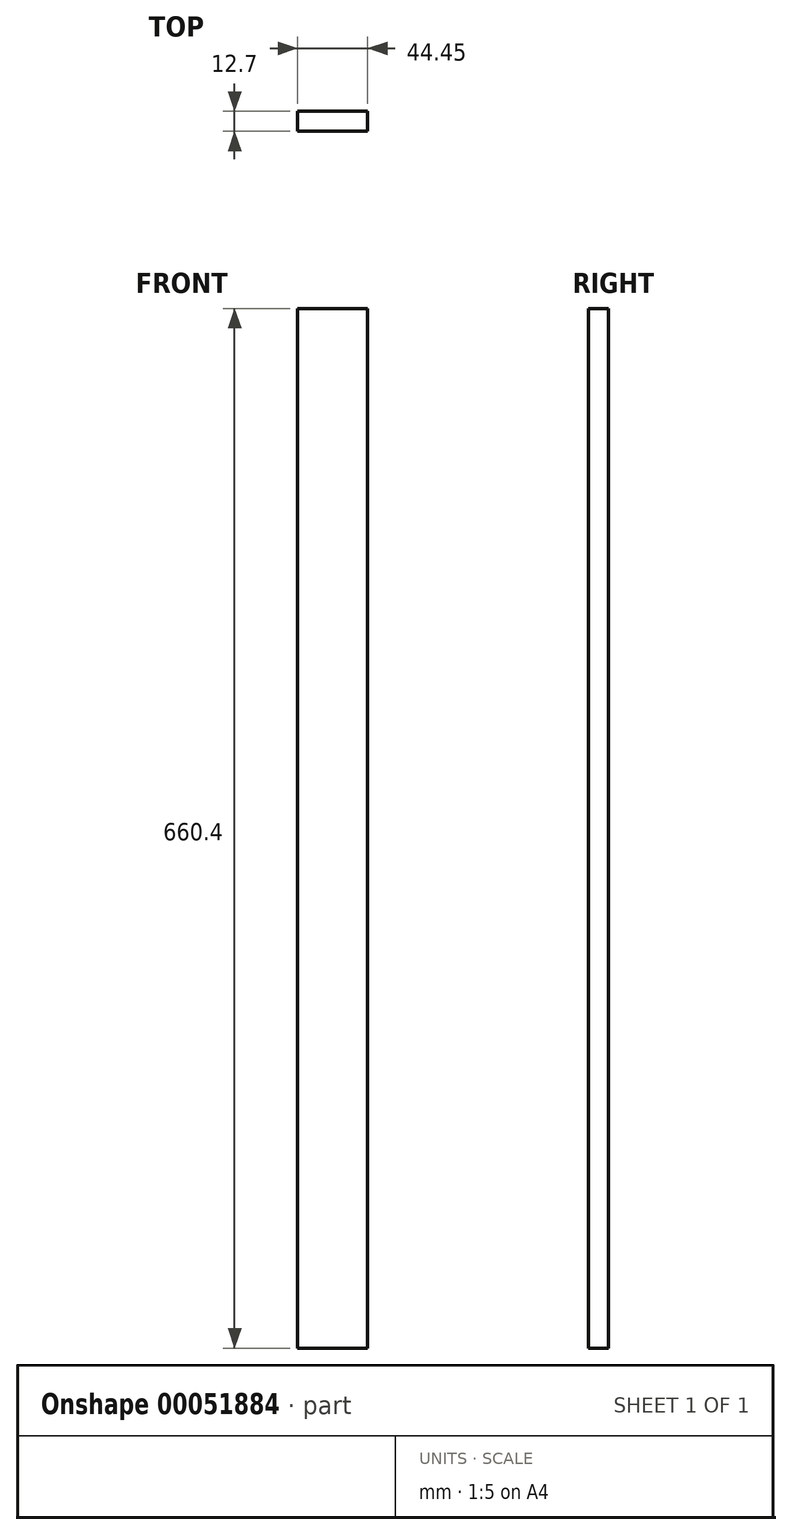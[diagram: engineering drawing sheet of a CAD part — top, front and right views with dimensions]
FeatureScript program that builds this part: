
annotation { "Feature Type Name" : "Feature", "Feature Type Description" : "" }
export const myFeature = defineFeature(function(context is Context, id is Id, definition is map)
    precondition{}
    {
        {
            var Q0;
            Q0=qCreatedBy(makeId("Front.planeOp"),FACE);
            var sketch = newSketch(context, id + "F0", { "sketchPlane" : qUnion([Q0])});
            skLineSegment(sketch, "E0.bottom", {"start": v(0, 0) * mm, "end": v(44.45, 0) * mm});
            skLineSegment(sketch, "E0.top", {"start": v(0, 660.4) * mm, "end": v(44.45, 660.4) * mm});
            skLineSegment(sketch, "E0.left", {"start": v(0, 0) * mm, "end": v(0, 660.4) * mm});
            skLineSegment(sketch, "E0.right", {"start": v(44.45, 0) * mm, "end": v(44.45, 660.4) * mm});
            skSolve(sketch);
        }
        {
            var Q0;
            Q0=makeQuery(id+"F0.imprint","IMPRINT",FACE,{"disambiguationData":[TD([[makeQuery(id+"F0.imprint","IMPRINT",EDGE,{"derivedFrom":sQuery(id+"F0.wireOp",EDGE,"E0.bottom")}),1.0]])]});
            extrude(context, id + "F1", {"entities" : qUnion([Q0]), "depth" : 12.7 * mm});
        }
    });
